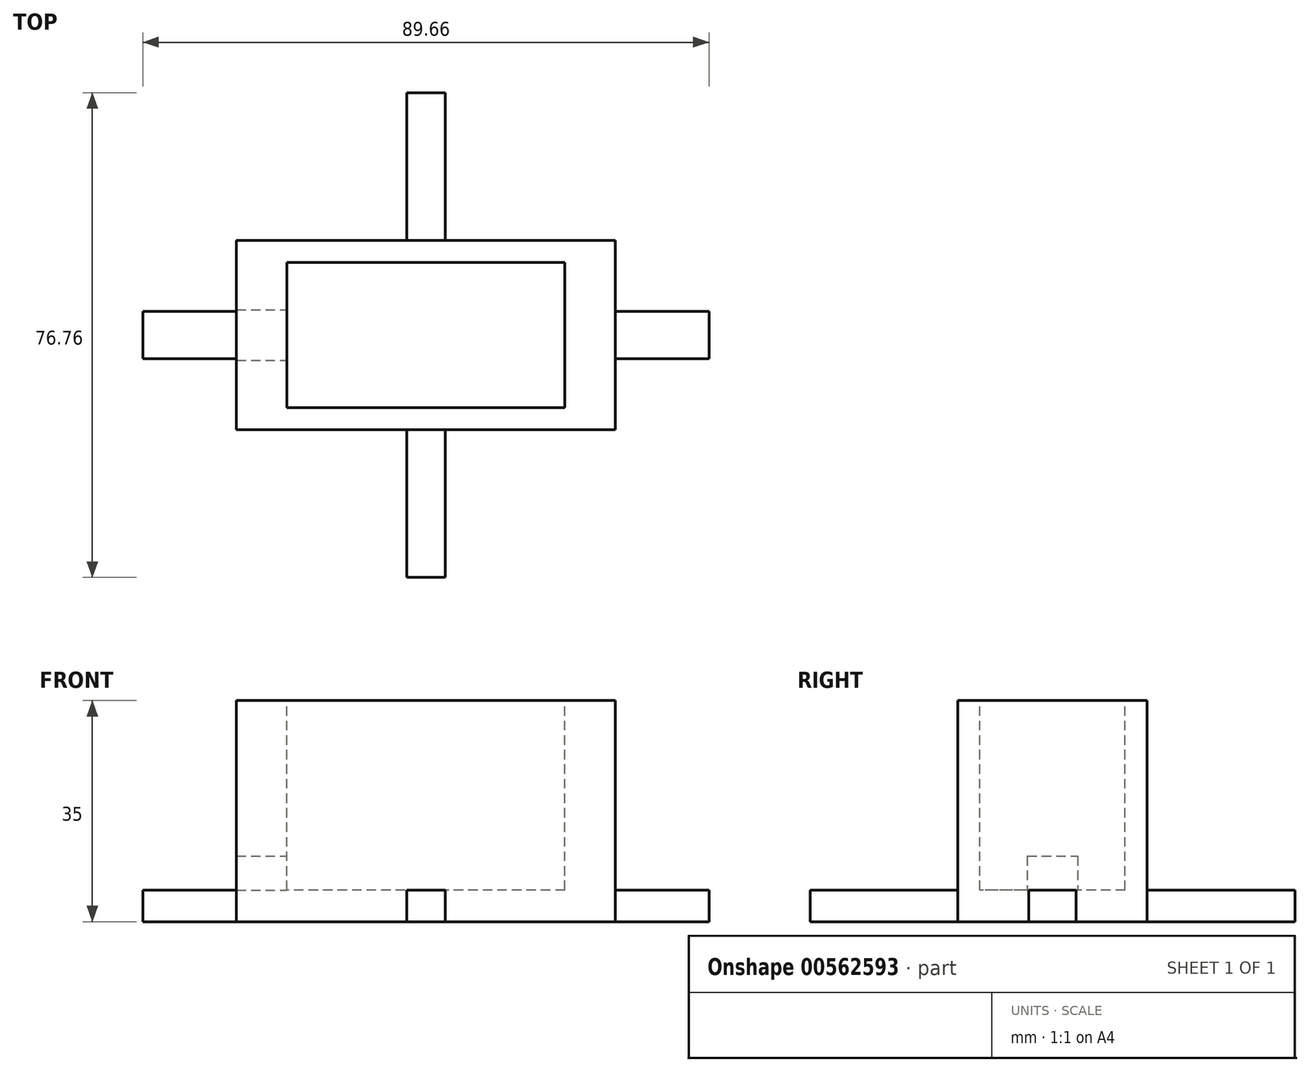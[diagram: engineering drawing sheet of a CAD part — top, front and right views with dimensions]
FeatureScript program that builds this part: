
annotation { "Feature Type Name" : "Feature", "Feature Type Description" : "" }
export const myFeature = defineFeature(function(context is Context, id is Id, definition is map)
    precondition{}
    {
        {
            var Q0;
            Q0=qCreatedBy(makeId("Top.planeOp"),FACE);
            var sketch = newSketch(context, id + "F0", { "sketchPlane" : qUnion([Q0])});
            skLineSegment(sketch, "E0.bottom", {"start": v(30, -15) * mm, "end": v(-30, -15) * mm});
            skLineSegment(sketch, "E0.top", {"start": v(30, 15) * mm, "end": v(-30, 15) * mm});
            skLineSegment(sketch, "E0.left", {"start": v(30, -15) * mm, "end": v(30, 15) * mm});
            skLineSegment(sketch, "E0.right", {"start": v(-30, -15) * mm, "end": v(-30, 15) * mm});
            skPoint(sketch, "E0.middle", {"position": v(0, 0) * mm});
            skLineSegment(sketch, "E1.bottom", {"start": v(44.83, -3.74) * mm, "end": v(-44.83, -3.74) * mm});
            skLineSegment(sketch, "E1.top", {"start": v(44.83, 3.74) * mm, "end": v(-44.83, 3.74) * mm});
            skLineSegment(sketch, "E1.left", {"start": v(44.83, -3.74) * mm, "end": v(44.83, 3.74) * mm});
            skLineSegment(sketch, "E1.right", {"start": v(-44.83, -3.74) * mm, "end": v(-44.83, 3.74) * mm});
            skLineSegment(sketch, "E2.bottom", {"start": v(3.06, -38.38) * mm, "end": v(-3.06, -38.38) * mm});
            skLineSegment(sketch, "E2.top", {"start": v(3.06, 38.38) * mm, "end": v(-3.06, 38.38) * mm});
            skLineSegment(sketch, "E2.left", {"start": v(3.06, -38.38) * mm, "end": v(3.06, 38.38) * mm});
            skLineSegment(sketch, "E2.right", {"start": v(-3.06, -38.38) * mm, "end": v(-3.06, 38.38) * mm});
            skSolve(sketch);
        }
        {
            var Q0;
            {var subQ0=sQuery(id+"F0.wireOp",EDGE,"E0.left");var subQ1=sQuery(id+"F0.wireOp",EDGE,"E0.top");var subQ2=makeQuery(id+"F0.imprint","INTERSECT",VERTEX,{"derivedFrom":[subQ1,subQ0]});Q0=makeQuery(id+"F0.imprint","IMPRINT",FACE,{"disambiguationData":[TD([[makeQuery(id+"F0.imprint","IMPRINT",EDGE,{"disambiguationData":[TD([[subQ2,-1.0]])],"derivedFrom":subQ1}),1.0]])]});}
            var Q1;
            {var subQ0=sQuery(id+"F0.wireOp",EDGE,"E0.left");var subQ1=sQuery(id+"F0.wireOp",EDGE,"E0.bottom");var subQ2=makeQuery(id+"F0.imprint","INTERSECT",VERTEX,{"derivedFrom":[subQ1,subQ0]});Q1=makeQuery(id+"F0.imprint","IMPRINT",FACE,{"disambiguationData":[TD([[makeQuery(id+"F0.imprint","IMPRINT",EDGE,{"disambiguationData":[TD([[subQ2,-1.0]])],"derivedFrom":subQ1}),-1.0]])]});}
            var Q2;
            {var subQ0=sQuery(id+"F0.wireOp",EDGE,"E1.bottom");var subQ1=sQuery(id+"F0.wireOp",EDGE,"E0.left");var subQ2=makeQuery(id+"F0.imprint","INTERSECT",VERTEX,{"derivedFrom":[subQ1,subQ0]});Q2=makeQuery(id+"F0.imprint","IMPRINT",FACE,{"disambiguationData":[TD([[makeQuery(id+"F0.imprint","IMPRINT",EDGE,{"disambiguationData":[TD([[subQ2,-1.0]])],"derivedFrom":subQ1}),1.0]])]});}
            var Q3;
            {var subQ0=sQuery(id+"F0.wireOp",EDGE,"E0.right");var subQ1=sQuery(id+"F0.wireOp",EDGE,"E0.top");var subQ2=makeQuery(id+"F0.imprint","INTERSECT",VERTEX,{"derivedFrom":[subQ1,subQ0]});Q3=makeQuery(id+"F0.imprint","IMPRINT",FACE,{"disambiguationData":[TD([[makeQuery(id+"F0.imprint","IMPRINT",EDGE,{"disambiguationData":[TD([[subQ2,1.0]])],"derivedFrom":subQ1}),1.0]])]});}
            var Q4;
            {var subQ0=sQuery(id+"F0.wireOp",EDGE,"E1.bottom");var subQ1=sQuery(id+"F0.wireOp",EDGE,"E0.right");var subQ2=makeQuery(id+"F0.imprint","INTERSECT",VERTEX,{"derivedFrom":[subQ1,subQ0]});Q4=makeQuery(id+"F0.imprint","IMPRINT",FACE,{"disambiguationData":[TD([[makeQuery(id+"F0.imprint","IMPRINT",EDGE,{"disambiguationData":[TD([[subQ2,-1.0]])],"derivedFrom":subQ1}),-1.0]])]});}
            var Q5;
            {var subQ0=sQuery(id+"F0.wireOp",EDGE,"E0.right");var subQ1=sQuery(id+"F0.wireOp",EDGE,"E0.bottom");var subQ2=makeQuery(id+"F0.imprint","INTERSECT",VERTEX,{"derivedFrom":[subQ1,subQ0]});Q5=makeQuery(id+"F0.imprint","IMPRINT",FACE,{"disambiguationData":[TD([[makeQuery(id+"F0.imprint","IMPRINT",EDGE,{"disambiguationData":[TD([[subQ2,1.0]])],"derivedFrom":subQ1}),-1.0]])]});}
            var Q6;
            {var subQ0=sQuery(id+"F0.wireOp",EDGE,"E2.left");var subQ1=sQuery(id+"F0.wireOp",EDGE,"E0.bottom");var subQ2=makeQuery(id+"F0.imprint","INTERSECT",VERTEX,{"derivedFrom":[subQ1,subQ0]});Q6=makeQuery(id+"F0.imprint","IMPRINT",FACE,{"disambiguationData":[TD([[makeQuery(id+"F0.imprint","IMPRINT",EDGE,{"disambiguationData":[TD([[subQ2,-1.0]])],"derivedFrom":subQ1}),-1.0]])]});}
            var Q7;
            {var subQ0=sQuery(id+"F0.wireOp",EDGE,"E2.left");var subQ1=sQuery(id+"F0.wireOp",EDGE,"E1.bottom");var subQ2=makeQuery(id+"F0.imprint","INTERSECT",VERTEX,{"derivedFrom":[subQ1,subQ0]});Q7=makeQuery(id+"F0.imprint","IMPRINT",FACE,{"disambiguationData":[TD([[makeQuery(id+"F0.imprint","IMPRINT",EDGE,{"disambiguationData":[TD([[subQ2,-1.0]])],"derivedFrom":subQ1}),-1.0]])]});}
            var Q8;
            {var subQ0=sQuery(id+"F0.wireOp",EDGE,"E2.left");var subQ1=sQuery(id+"F0.wireOp",EDGE,"E0.top");var subQ2=makeQuery(id+"F0.imprint","INTERSECT",VERTEX,{"derivedFrom":[subQ1,subQ0]});Q8=makeQuery(id+"F0.imprint","IMPRINT",FACE,{"disambiguationData":[TD([[makeQuery(id+"F0.imprint","IMPRINT",EDGE,{"disambiguationData":[TD([[subQ2,-1.0]])],"derivedFrom":subQ1}),1.0]])]});}
            extrude(context, id + "F1", {"entities" : qUnion([Q0, Q1, Q2, Q3, Q4, Q5, Q6, Q7, Q8]), "depth" : 35 * mm, "offsetDistance" : 25 * mm});
        }
        {
            var Q0;
            {var subQ5=sQuery(id+"F0.wireOp",EDGE,"E2.top");Q0=makeQuery(id+"F0.imprint","IMPRINT",FACE,{"disambiguationData":[TD([[makeQuery(id+"F0.imprint","IMPRINT",EDGE,{"derivedFrom":subQ5}),1.0]])]});}
            var Q1;
            {var subQ5=sQuery(id+"F0.wireOp",EDGE,"E1.left");Q1=makeQuery(id+"F0.imprint","IMPRINT",FACE,{"disambiguationData":[TD([[makeQuery(id+"F0.imprint","IMPRINT",EDGE,{"derivedFrom":subQ5}),1.0]])]});}
            var Q2;
            {var subQ5=sQuery(id+"F0.wireOp",EDGE,"E1.right");Q2=makeQuery(id+"F0.imprint","IMPRINT",FACE,{"disambiguationData":[TD([[makeQuery(id+"F0.imprint","IMPRINT",EDGE,{"derivedFrom":subQ5}),-1.0]])]});}
            var Q3;
            {var subQ5=sQuery(id+"F0.wireOp",EDGE,"E2.bottom");Q3=makeQuery(id+"F0.imprint","IMPRINT",FACE,{"disambiguationData":[TD([[makeQuery(id+"F0.imprint","IMPRINT",EDGE,{"derivedFrom":subQ5}),-1.0]])]});}
            extrude(context, id + "F2", {"entities" : qUnion([Q0, Q1, Q2, Q3]), "operationType" : NewBodyOperationType.ADD, "depth" : 5 * mm, "offsetDistance" : 25 * mm});
        }
        {
            var Q0;
            Q0=makeQuery(id+"F1.opExtrude","CAP_FACE",FACE,{"disambiguationData":[OSD([sQuery(id+"F0.wireOp",EDGE,"E0.bottom"),sQuery(id+"F0.wireOp",EDGE,"E0.top"),sQuery(id+"F0.wireOp",EDGE,"E0.left"),sQuery(id+"F0.wireOp",EDGE,"E0.right")])],"isStart":false});
            var sketch = newSketch(context, id + "F3", { "sketchPlane" : qUnion([Q0])});
            skPoint(sketch, "E3.middle", {"position": v(1.19, 0) * mm});
            skLineSegment(sketch, "E4.bottom", {"start": v(22, 11.5) * mm, "end": v(-22, 11.5) * mm});
            skLineSegment(sketch, "E4.top", {"start": v(22, -11.5) * mm, "end": v(-22, -11.5) * mm});
            skLineSegment(sketch, "E4.left", {"start": v(22, 11.5) * mm, "end": v(22, -11.5) * mm});
            skLineSegment(sketch, "E4.right", {"start": v(-22, 11.5) * mm, "end": v(-22, -11.5) * mm});
            skPoint(sketch, "E4.middle", {"position": v(0, 0) * mm});
            skSolve(sketch);
        }
        {
            var Q0;
            Q0=makeQuery(id+"F3.imprint","IMPRINT",FACE,{"disambiguationData":[TD([[makeQuery(id+"F3.imprint","IMPRINT",EDGE,{"derivedFrom":sQuery(id+"F3.wireOp",EDGE,"E4.bottom")}),1.0]])]});
            extrude(context, id + "F4", {"entities" : qUnion([Q0]), "operationType" : NewBodyOperationType.REMOVE, "oppositeDirection" : true, "depth" : 30 * mm, "offsetDistance" : 25 * mm});
        }
        {
            var Q0;
            Q0=makeQuery(id+"F4.boolean.opBoolean","COPY",FACE,{"derivedFrom":makeQuery(id+"F4.opExtrude","SWEPT_FACE",FACE,{"disambiguationData":[OSD([sQuery(id+"F3.wireOp",EDGE,"E4.right")])]})});
            var sketch = newSketch(context, id + "F5", { "sketchPlane" : qUnion([Q0])});
            skLineSegment(sketch, "E5", {"start": v(0, 5) * mm, "end": v(0, 7.7) * mm});
            skLineSegment(sketch, "E6", {"start": v(0, 7.7) * mm, "end": v(0, 35) * mm});
            skLineSegment(sketch, "E7.bottom", {"start": v(4, 5) * mm, "end": v(-4, 5) * mm});
            skLineSegment(sketch, "E7.top", {"start": v(4, 10.38) * mm, "end": v(-4, 10.38) * mm});
            skLineSegment(sketch, "E7.left", {"start": v(4, 5) * mm, "end": v(4, 10.38) * mm});
            skLineSegment(sketch, "E7.right", {"start": v(-4, 5) * mm, "end": v(-4, 10.38) * mm});
            skPoint(sketch, "E7.middle", {"position": v(0, 7.7) * mm});
            skSolve(sketch);
        }
        {
            var Q0;
            {var subQ1=sQuery(id+"F5.wireOp",EDGE,"E5");Q0=makeQuery(id+"F5.imprint","IMPRINT",FACE,{"disambiguationData":[TD([[makeQuery(id+"F5.imprint","IMPRINT",EDGE,{"derivedFrom":subQ1}),1.0]])]});}
            var Q1;
            {var subQ1=sQuery(id+"F5.wireOp",EDGE,"E5");Q1=makeQuery(id+"F5.imprint","IMPRINT",FACE,{"disambiguationData":[TD([[makeQuery(id+"F5.imprint","IMPRINT",EDGE,{"derivedFrom":subQ1}),-1.0]])]});}
            extrude(context, id + "F6", {"entities" : qUnion([Q0, Q1]), "operationType" : NewBodyOperationType.REMOVE, "oppositeDirection" : true, "depth" : 25 * mm, "offsetDistance" : 25 * mm});
        }
    });
